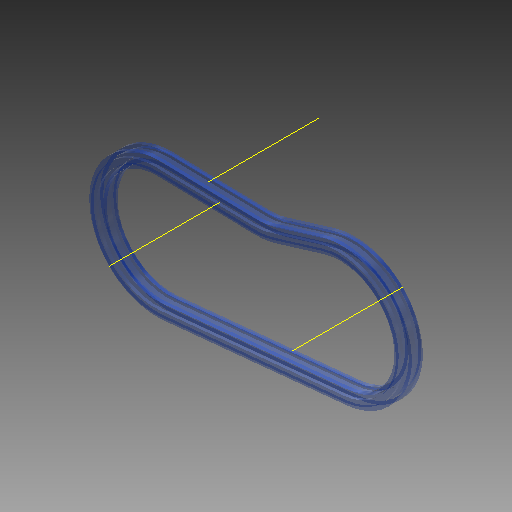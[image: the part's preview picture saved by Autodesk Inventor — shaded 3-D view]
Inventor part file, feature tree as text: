
AUTODESK INVENTOR PART (.ipt)
format: ipt  version: 2017 (Build 210142000, 142)  size: 216,576 bytes
history: native  units: mm
features: other x6, plane x2, pattern_linear x1
ambient origin geometry x8: Origin, YZ Plane, XZ Plane, XY Plane, X Axis, Y Axis, Z Axis, Center Point
bodies: Solid1 (feature_tree), Solid (feature_tree)
feature tree (9):
  other  "Work Axis1"
  other  "Work Axis2"
  other  "Work Axis3"
  plane  "Work Plane2"
  plane  "Work Plane3"
  other  "Path"
  other  "Section Plane"
  pattern_linear  "Strand Pattern"  Spacing1=0.0mm  [1 undecoded]
  other  "Section Sketch"
note: 1 required parameter value undecoded (feature->parameter linkage not recoverable at this tier; creation-order binding heuristic only, values carry confidence <= 0.55)
